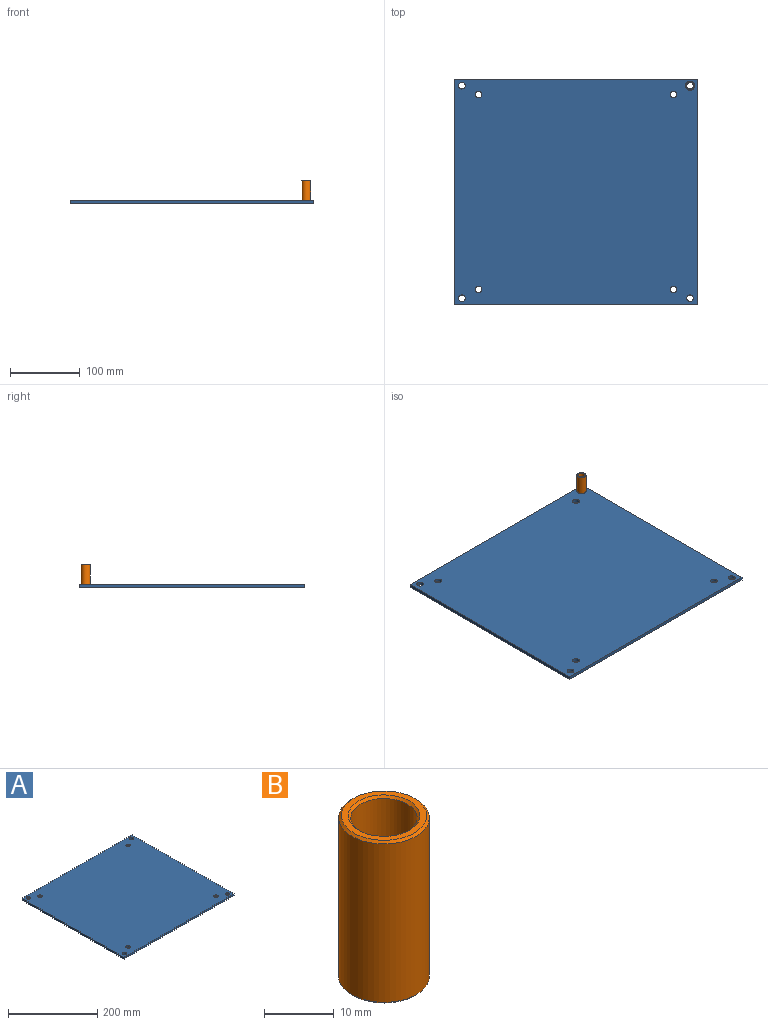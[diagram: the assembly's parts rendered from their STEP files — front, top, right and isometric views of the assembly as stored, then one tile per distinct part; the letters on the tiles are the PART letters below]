
ASSEMBLY  parts=2 mates=1
PART A: 14 faces, bbox 349.3x323.9x4.8 mm
  f0: plane 349.25x4.76mm, normal (0,1,0), area 1663.3mm2, adj f1,f10,f12,f13
  f1: plane 323.85x4.76mm, normal (-1,0,0), area 1542.3mm2, adj f0,f2,f12,f13
  f2: plane 349.25x4.76mm, normal (0,-1,0), area 1663.3mm2, adj f1,f10,f12,f13
  f3: cylinder r=4.76mm len=9.53mm, axis (0,0,-1), area 142.5mm2, adj f12,f13
  f4: cylinder r=4.76mm len=9.53mm, axis (0,0,-1), area 142.5mm2, adj f12,f13
  f5: cylinder r=4.76mm len=9.53mm, axis (0,0,-1), area 142.5mm2, adj f12,f13
  f6: cylinder r=4.76mm len=9.53mm, axis (0,0,-1), area 142.5mm2, adj f12,f13
  f7: cylinder r=4.76mm len=9.53mm, axis (0,0,-1), area 142.5mm2, adj f12,f13
  f8: cylinder r=4.76mm len=9.53mm, axis (0,0,-1), area 142.5mm2, adj f12,f13
  f9: cylinder r=4.76mm len=9.53mm, axis (0,0,-1), area 142.5mm2, adj f12,f13
  f10: plane 323.85x4.76mm, normal (1,0,0), area 1542.3mm2, adj f0,f2,f12,f13
  f11: cylinder r=4.76mm len=9.53mm, axis (0,0,-1), area 142.5mm2, adj f12,f13
  f12: plane 349.25x323.85mm, normal (0,0,1), area 112534.6mm2, adj f0,f1,f2,f3,f4,f5,f6,f7
  f13: plane 349.25x323.85mm, normal (0,0,-1), area 112534.6mm2, adj f0,f1,f2,f3,f4,f5,f6,f7
PART B: 8 faces, bbox 13x13x28.6 mm
  f0: cylinder r=4.76mm len=27.81mm, axis (0,0,-1), area 832.3mm2, adj f5,f6
  f1: cylinder r=6.5mm len=27.81mm, axis (0,0,-1), area 1136.3mm2, adj f4,f7
  f2: plane 12.24x12.24mm, normal (0,0,1), area 34.6mm2, adj f6,f7
  f3: plane 12.24x12.24mm, normal (0,0,-1), area 34.6mm2, adj f4,f5
  f4: cone r=6.5mm half-angle=45deg, axis (0,0,1), area 21.4mm2, adj f1,f3
  f5: cone r=5.14mm half-angle=45deg, axis (0,0,-1), area 16.8mm2, adj f0,f3
  f6: cone r=4.76mm half-angle=45deg, axis (0,0,1), area 16.8mm2, adj f0,f2
  f7: cone r=6.12mm half-angle=45deg, axis (0,0,-1), area 21.4mm2, adj f1,f2
PLACE A t=(-2.22,-19.78,3.74)mm
PLACE B t=(161.29,132.62,8.12)mm
MATE fastened A.f8 <-> B.f0  axis (0,0,1) through (161.29,132.62,8.5)mm
